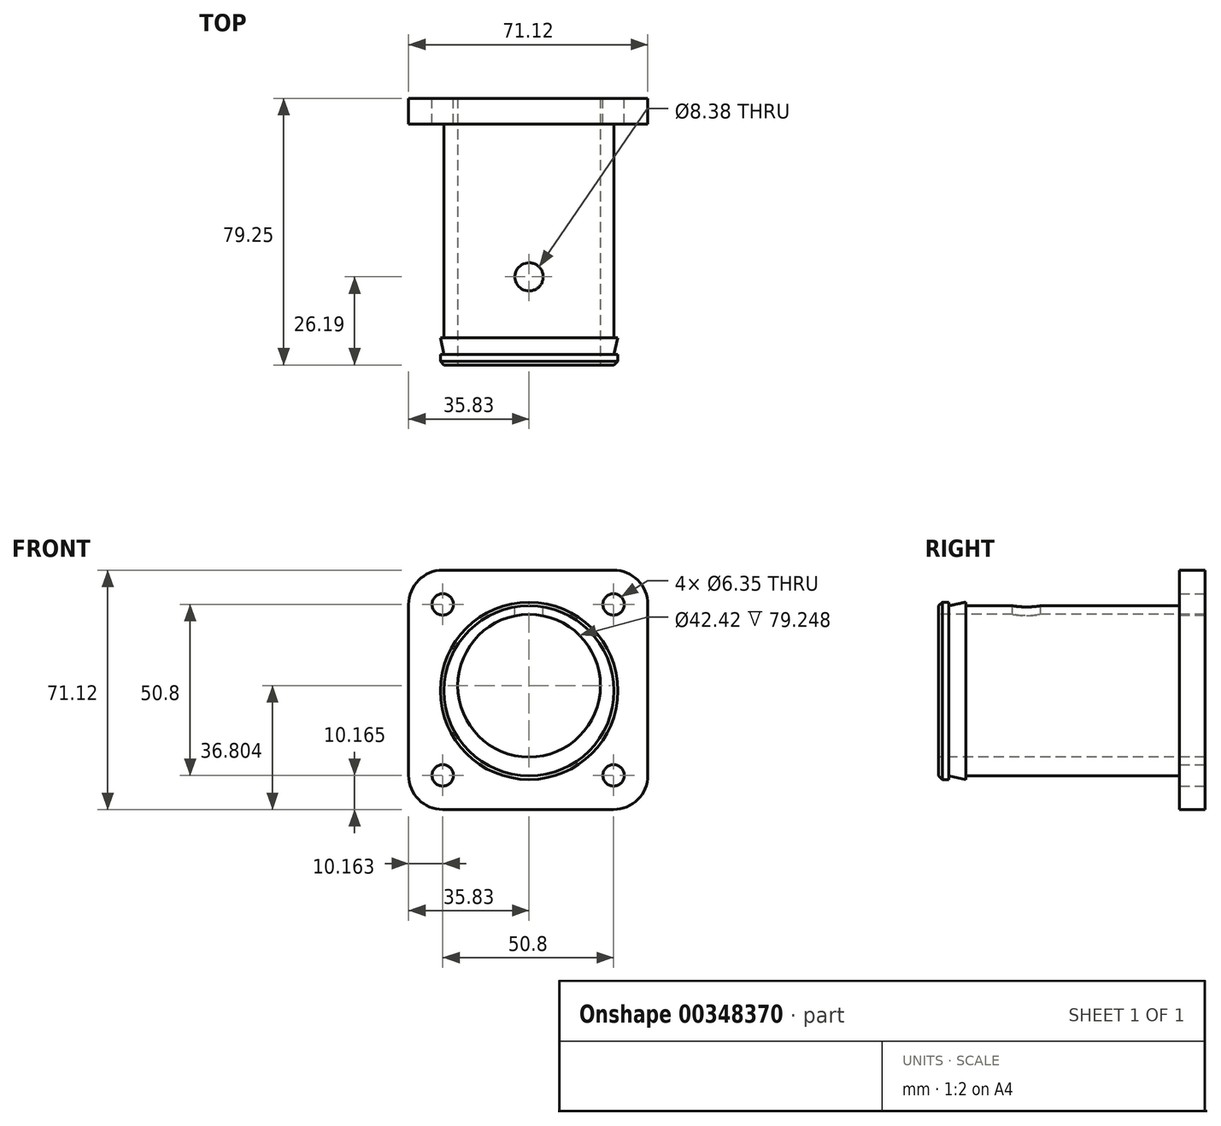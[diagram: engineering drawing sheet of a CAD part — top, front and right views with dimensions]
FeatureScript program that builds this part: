
annotation { "Feature Type Name" : "Feature", "Feature Type Description" : "" }
export const myFeature = defineFeature(function(context is Context, id is Id, definition is map)
    precondition{}
    {
        {
            var Q0;
            Q0=qCreatedBy(makeId("Front.planeOp"),FACE);
            var sketch = newSketch(context, id + "F0", { "sketchPlane" : qUnion([Q0])});
            skCircle(sketch, "E0", {"center": v(0, 3.17) * mm, "radius": 21.2 * mm});
            skCircle(sketch, "E1", {"center": v(0, 1.65) * mm, "radius": 25.27 * mm});
            skLineSegment(sketch, "E2", {"start": v(0, 26.92) * mm, "end": v(0, 24.38) * mm});
            skSolve(sketch);
        }
        {
            var Q0;
            Q0=makeQuery(id+"F0.imprint","IMPRINT",FACE,{"disambiguationData":[TD([[makeQuery(id+"F0.imprint","IMPRINT",EDGE,{"derivedFrom":sQuery(id+"F0.wireOp",EDGE,"E0")}),-1.0]])]});
            extrude(context, id + "F1", {"entities" : qUnion([Q0]), "oppositeDirection" : true, "depth" : 79.25 * mm});
        }
        {
            var Q0;
            Q0=makeQuery(id+"F1.opExtrude","CAP_FACE",FACE,{"disambiguationData":[OSD([sQuery(id+"F0.wireOp",EDGE,"E0"),sQuery(id+"F0.wireOp",EDGE,"E1")])],"isStart":true});
            var sketch = newSketch(context, id + "F2", { "sketchPlane" : qUnion([Q0])});
            skLineSegment(sketch, "E3", {"start": v(0, 26.92) * mm, "end": v(-24.13, 26.92) * mm});
            skLineSegment(sketch, "E4.MirrorCS", {"start": v(0, 26.92) * mm, "end": v(24.13, 26.92) * mm});
            skLineSegment(sketch, "E5.MirrorCS", {"start": v(24.13, 26.92) * mm, "end": v(24.13, 20.88) * mm});
            skLineSegment(sketch, "E6.MirrorCS", {"start": v(-24.13, 26.92) * mm, "end": v(-24.13, 20.88) * mm});
            skLineSegment(sketch, "E7", {"start": v(-24.13, 20.88) * mm, "end": v(-16.4, 20.88) * mm});
            skLineSegment(sketch, "E8.MirrorCS", {"start": v(24.13, 20.88) * mm, "end": v(16.4, 20.88) * mm});
            skSolve(sketch);
        }
        {
            var Q0;
            {var subQ0=sQuery(id+"F2.wireOp",EDGE,"E5.MirrorCS");Q0=makeQuery(id+"F2.imprint","IMPRINT",FACE,{"disambiguationData":[TD([[makeQuery(id+"F2.imprint","IMPRINT",EDGE,{"derivedFrom":subQ0}),-1.0]])]});}
            var Q1;
            {var subQ0=sQuery(id+"F2.wireOp",EDGE,"E3");Q1=makeQuery(id+"F2.imprint","IMPRINT",FACE,{"disambiguationData":[TD([[makeQuery(id+"F2.imprint","IMPRINT",EDGE,{"derivedFrom":subQ0}),1.0]])]});}
            extrude(context, id + "F3", {"entities" : qUnion([Q0, Q1]), "operationType" : NewBodyOperationType.REMOVE, "oppositeDirection" : true, "depth" : 11.25 * mm});
        }
        {
            var Q0;
            Q0=qCreatedBy(makeId("Right.planeOp"),FACE);
            var sketch = newSketch(context, id + "F4", { "sketchPlane" : qUnion([Q0])});
            skLineSegment(sketch, "E9.0.0", {"start": v(0, -23.62) * mm, "end": v(0, 26.92) * mm});
            skLineSegment(sketch, "E10", {"start": v(0, 26.92) * mm, "end": v(1.14, 28.01) * mm});
            skLineSegment(sketch, "E11", {"start": v(1.14, 28.01) * mm, "end": v(3.1, 28.01) * mm});
            skLineSegment(sketch, "E12", {"start": v(0, 26.92) * mm, "end": v(16.15, 26.92) * mm});
            skLineSegment(sketch, "E13", {"start": v(3.1, 28.01) * mm, "end": v(3.1, 26.92) * mm});
            skLineSegment(sketch, "E14", {"start": v(8.08, 26.92) * mm, "end": v(8.08, 28.01) * mm});
            skLineSegment(sketch, "E15", {"start": v(3.1, 26.92) * mm, "end": v(8.08, 28.01) * mm});
            skSolve(sketch);
        }
        {
            var Q0;
            {var subQ0=sQuery(id+"F4.wireOp",EDGE,"E10");Q0=makeQuery(id+"F4.imprint","IMPRINT",FACE,{"disambiguationData":[TD([[makeQuery(id+"F4.imprint","IMPRINT",EDGE,{"derivedFrom":subQ0}),-1.0]])]});}
            var Q1;
            {var subQ2=sQuery(id+"F4.wireOp",EDGE,"E14");Q1=makeQuery(id+"F4.imprint","IMPRINT",FACE,{"disambiguationData":[TD([[makeQuery(id+"F4.imprint","IMPRINT",EDGE,{"derivedFrom":subQ2}),1.0]])]});}
            var Q2;
            {var subQ2=sQuery(id+"F4.wireOp",EDGE,"DYTCZVRh-lFz5-yrRv-6JYv-kieStgS32U4B");Q2=makeQuery(id+"F4.imprint","IMPRINT",FACE,{"disambiguationData":[TD([[makeQuery(id+"F4.imprint","IMPRINT",EDGE,{"derivedFrom":subQ2}),1.0]])]});}
            var Q3;
            Q3=makeQuery(id+"F1.opExtrude","CAP_EDGE",EDGE,{"disambiguationData":[OSD([sQuery(id+"F0.wireOp",EDGE,"E1")])],"isStart":true});
            revolve(context, id + "F5", {"operationType" : NewBodyOperationType.ADD, "entities" : qUnion([Q0, Q1, Q2]), "axis" : qUnion([Q3]), "revolveType" : RevolveType.FULL});
        }
        {
            var Q0;
            Q0=makeQuery(id+"F1.opExtrude","CAP_FACE",FACE,{"disambiguationData":[OSD([sQuery(id+"F0.wireOp",EDGE,"E0"),sQuery(id+"F0.wireOp",EDGE,"E1")])],"isStart":false});
            var sketch = newSketch(context, id + "F6", { "sketchPlane" : qUnion([Q0])});
            skCircle(sketch, "E16.0", {"center": v(0, 1.65) * mm, "radius": 25.27 * mm});
            skLineSegment(sketch, "E17.bottom", {"start": v(25.67, -33.63) * mm, "end": v(-25.13, -33.63) * mm});
            skLineSegment(sketch, "E17.top", {"start": v(25.67, 37.5) * mm, "end": v(-25.13, 37.5) * mm});
            skLineSegment(sketch, "E17.left", {"start": v(35.83, -23.47) * mm, "end": v(35.83, 27.33) * mm});
            skLineSegment(sketch, "E17.right", {"start": v(-35.3, -23.47) * mm, "end": v(-35.3, 27.33) * mm});
            skPoint(sketch, "E18.visualSharp", {"position": v(-35.3, 37.5) * mm});
            skArc(sketch, "E18.filletArc", {"start": v(-25.13, 37.5) * mm, "mid": v(-32.32, 34.52) * mm, "end": v(-35.3, 27.33) * mm});
            skPoint(sketch, "E19.visualSharp", {"position": v(35.83, 37.5) * mm});
            skArc(sketch, "E19.filletArc", {"start": v(35.83, 27.33) * mm, "mid": v(32.85, 34.52) * mm, "end": v(25.67, 37.5) * mm});
            skPoint(sketch, "E20.visualSharp", {"position": v(35.83, -33.63) * mm});
            skArc(sketch, "E20.filletArc", {"start": v(25.67, -33.63) * mm, "mid": v(32.85, -30.65) * mm, "end": v(35.83, -23.47) * mm});
            skPoint(sketch, "E21.visualSharp", {"position": v(-35.3, -33.63) * mm});
            skArc(sketch, "E21.filletArc", {"start": v(-35.3, -23.47) * mm, "mid": v(-32.32, -30.65) * mm, "end": v(-25.13, -33.63) * mm});
            skCircle(sketch, "E22", {"center": v(-25.13, 27.33) * mm, "radius": 3.18 * mm});
            skCircle(sketch, "E23", {"center": v(25.67, 27.33) * mm, "radius": 3.18 * mm});
            skCircle(sketch, "E24", {"center": v(25.67, -23.47) * mm, "radius": 3.18 * mm});
            skCircle(sketch, "E25", {"center": v(-25.13, -23.47) * mm, "radius": 3.18 * mm});
            skCircle(sketch, "E26", {"center": v(0, 3.17) * mm, "radius": 21.2 * mm});
            skSolve(sketch);
        }
        {
            var Q0;
            Q0=makeQuery(id+"F6.imprint","IMPRINT",FACE,{"disambiguationData":[TD([[makeQuery(id+"F6.imprint","IMPRINT",EDGE,{"derivedFrom":sQuery(id+"F6.wireOp",EDGE,"E16.0")}),1.0]])]});
            var Q1;
            Q1=makeQuery(id+"F6.imprint","IMPRINT",FACE,{"disambiguationData":[TD([[makeQuery(id+"F6.imprint","IMPRINT",EDGE,{"derivedFrom":sQuery(id+"F6.wireOp",EDGE,"E16.0")}),-1.0]])]});
            extrude(context, id + "F7", {"entities" : qUnion([Q0, Q1]), "operationType" : NewBodyOperationType.ADD, "oppositeDirection" : true, "depth" : 7.62 * mm});
        }
        {
            var Q0;
            Q0=qCreatedBy(makeId("Top.planeOp"),FACE);
            cPlane(context, id + "F8", {"entities" : qUnion([Q0]), "cplaneType" : CPlaneType.OFFSET, "offset" : 28.45 * mm, "width" : 152.4 * mm, "height" : 152.4 * mm});
        }
        {
            var Q0;
            Q0=qCreatedBy(id+"F8.planeOp",FACE);
            var sketch = newSketch(context, id + "F9", { "sketchPlane" : qUnion([Q0])});
            skCircle(sketch, "E27", {"center": v(0, 26.19) * mm, "radius": 4.2 * mm});
            skSolve(sketch);
        }
        {
            var Q0;
            Q0=makeQuery(id+"F9.imprint","IMPRINT",FACE,{"disambiguationData":[TD([[makeQuery(id+"F9.imprint","IMPRINT",EDGE,{"derivedFrom":sQuery(id+"F9.wireOp",EDGE,"E27")}),1.0]])]});
            extrude(context, id + "F10", {"entities" : qUnion([Q0]), "operationType" : NewBodyOperationType.REMOVE, "oppositeDirection" : true, "depth" : 7.87 * mm});
        }
    });
